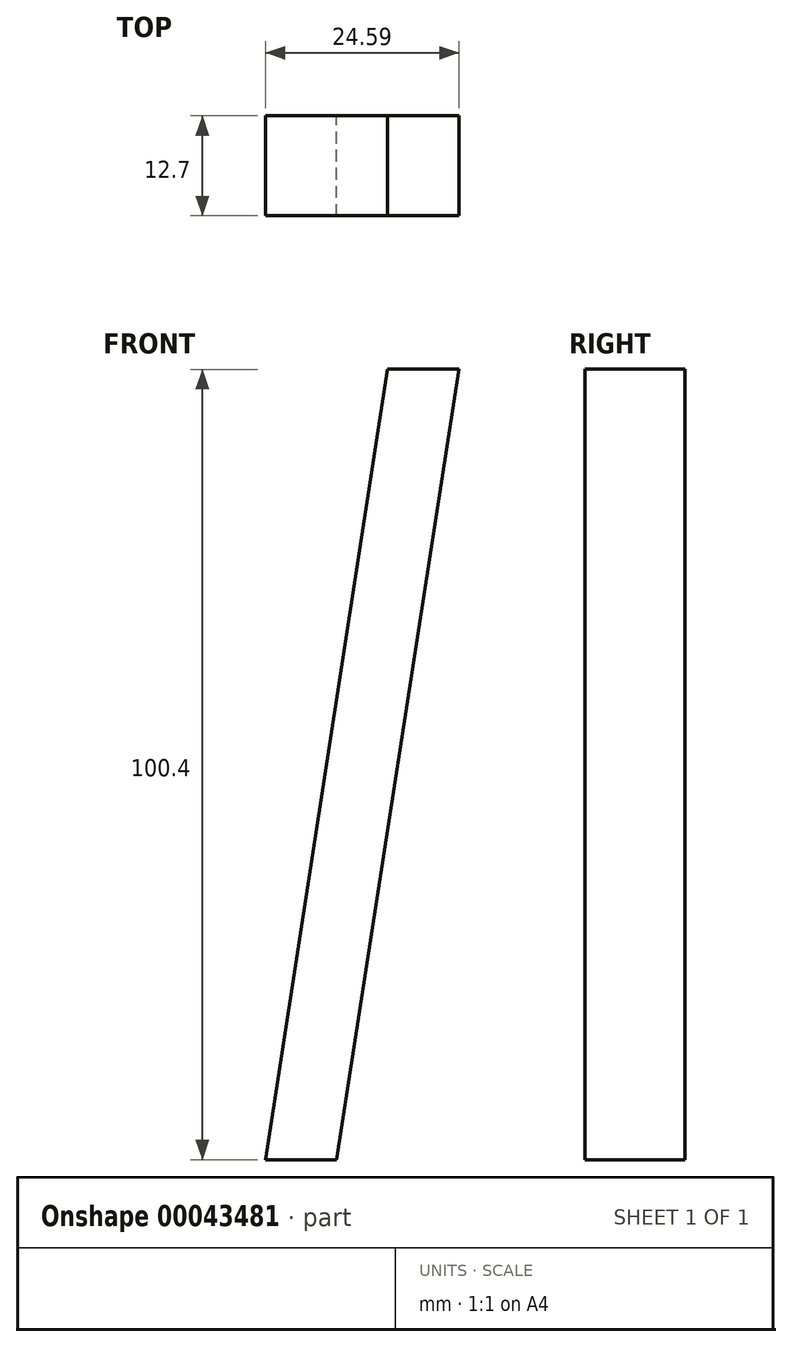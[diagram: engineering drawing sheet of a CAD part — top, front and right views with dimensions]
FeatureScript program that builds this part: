
annotation { "Feature Type Name" : "Feature", "Feature Type Description" : "" }
export const myFeature = defineFeature(function(context is Context, id is Id, definition is map)
    precondition{}
    {
        {
            var Q0;
            Q0=qCreatedBy(makeId("Front.planeOp"),FACE);
            var sketch = newSketch(context, id + "F0", { "sketchPlane" : qUnion([Q0])});
            skLineSegment(sketch, "E0", {"start": v(-15.3, 50.2) * mm, "end": v(-30.82, -50.2) * mm});
            skLineSegment(sketch, "E1", {"start": v(-30.82, -50.2) * mm, "end": v(-39.88, -50.2) * mm});
            skLineSegment(sketch, "E2", {"start": v(-39.88, -50.2) * mm, "end": v(-24.35, 50.2) * mm});
            skLineSegment(sketch, "E3", {"start": v(-24.35, 50.2) * mm, "end": v(-15.3, 50.2) * mm});
            skSolve(sketch);
        }
        {
            var Q0;
            Q0 = qSketchRegion(id + "F0", true);
            extrude(context, id + "F1", {"entities" : qUnion([Q0]), "depth" : 12.7 * mm});
        }
    });
